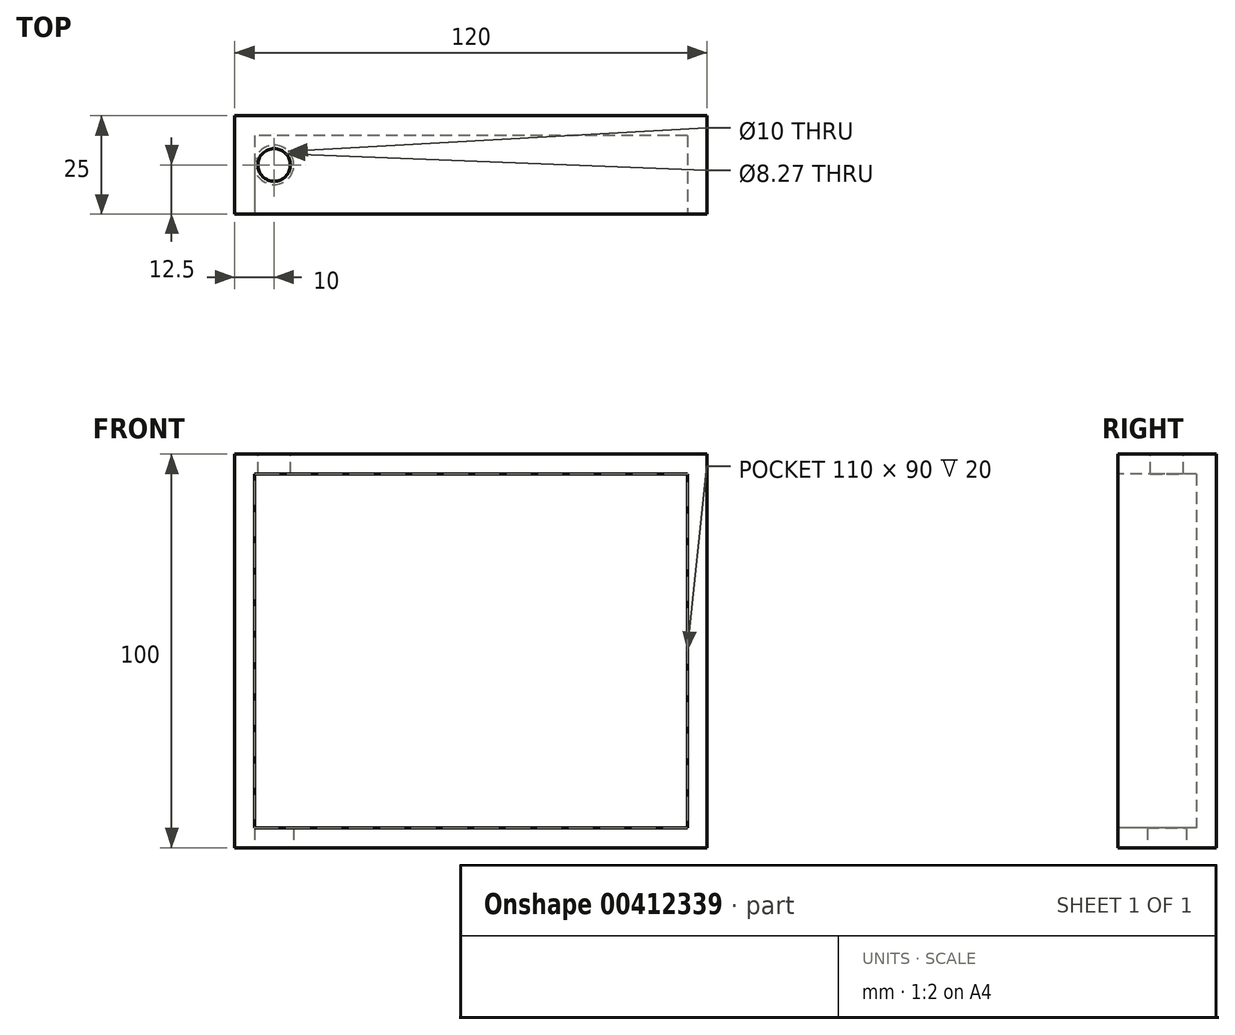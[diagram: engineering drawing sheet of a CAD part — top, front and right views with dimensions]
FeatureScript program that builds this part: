
annotation { "Feature Type Name" : "Feature", "Feature Type Description" : "" }
export const myFeature = defineFeature(function(context is Context, id is Id, definition is map)
    precondition{}
    {
        {
            var Q0;
            Q0=qCreatedBy(makeId("Front.planeOp"),FACE);
            var sketch = newSketch(context, id + "F0", { "sketchPlane" : qUnion([Q0])});
            skLineSegment(sketch, "E0.bottom", {"start": v(-60, 50) * mm, "end": v(60, 50) * mm});
            skLineSegment(sketch, "E0.top", {"start": v(-60, -50) * mm, "end": v(60, -50) * mm});
            skLineSegment(sketch, "E0.left", {"start": v(-60, 50) * mm, "end": v(-60, -50) * mm});
            skLineSegment(sketch, "E0.right", {"start": v(60, 50) * mm, "end": v(60, -50) * mm});
            skPoint(sketch, "E0.middle", {"position": v(0, 0) * mm});
            skSolve(sketch);
        }
        {
            var Q0;
            Q0=makeQuery(id+"F0.imprint","IMPRINT",FACE,{"disambiguationData":[TD([[makeQuery(id+"F0.imprint","IMPRINT",EDGE,{"derivedFrom":sQuery(id+"F0.wireOp",EDGE,"E0.bottom")}),-1.0]])]});
            extrude(context, id + "F1", {"entities" : qUnion([Q0]), "depth" : 25 * mm});
        }
        {
            var Q0;
            Q0=makeQuery(id+"F1.opExtrude","CAP_FACE",FACE,{"disambiguationData":[OSD([sQuery(id+"F0.wireOp",EDGE,"E0.bottom"),sQuery(id+"F0.wireOp",EDGE,"E0.top"),sQuery(id+"F0.wireOp",EDGE,"E0.left"),sQuery(id+"F0.wireOp",EDGE,"E0.right")])],"isStart":false});
            var sketch = newSketch(context, id + "F2", { "sketchPlane" : qUnion([Q0])});
            skLineSegment(sketch, "E1.bottom", {"start": v(55, 45) * mm, "end": v(-55, 45) * mm});
            skLineSegment(sketch, "E1.top", {"start": v(55, -45) * mm, "end": v(-55, -45) * mm});
            skLineSegment(sketch, "E1.left", {"start": v(55, 45) * mm, "end": v(55, -45) * mm});
            skLineSegment(sketch, "E1.right", {"start": v(-55, 45) * mm, "end": v(-55, -45) * mm});
            skPoint(sketch, "E1.middle", {"position": v(0, 0) * mm});
            skSolve(sketch);
        }
        {
            var Q0;
            Q0 = qSketchRegion(id + "F2", true);
            extrude(context, id + "F3", {"entities" : qUnion([Q0]), "operationType" : NewBodyOperationType.REMOVE, "oppositeDirection" : true, "depth" : 20 * mm});
        }
        {
            var Q0;
            Q0=makeQuery(id+"F1.opExtrude","SWEPT_FACE",FACE,{"disambiguationData":[OSD([sQuery(id+"F0.wireOp",EDGE,"E0.top")])]});
            var sketch = newSketch(context, id + "F4", { "sketchPlane" : qUnion([Q0])});
            skCircle(sketch, "E2", {"center": v(-50, 12.5) * mm, "radius": 5 * mm});
            skPoint(sketch, "E2.centerSnap0", {"position": v(-60, 12.5) * mm});
            skSolve(sketch);
        }
        {
            var Q0;
            Q0=makeQuery(id+"F4.imprint","IMPRINT",FACE,{"disambiguationData":[TD([[makeQuery(id+"F4.imprint","IMPRINT",EDGE,{"derivedFrom":sQuery(id+"F4.wireOp",EDGE,"E2")}),1.0]])]});
            var Q1;
            Q1=makeQuery(id+"F3.boolean.opBoolean","COPY",FACE,{"derivedFrom":makeQuery(id+"F3.opExtrude","SWEPT_FACE",FACE,{"disambiguationData":[OSD([sQuery(id+"F2.wireOp",EDGE,"E1.top")])]})});
            extrude(context, id + "F5", {"entities" : qUnion([Q0, Q1]), "operationType" : NewBodyOperationType.REMOVE, "oppositeDirection" : true, "depth" : 10 * mm});
        }
        {
            var Q0;
            Q0=makeQuery(id+"F1.opExtrude","SWEPT_FACE",FACE,{"disambiguationData":[OSD([sQuery(id+"F0.wireOp",EDGE,"E0.bottom")])]});
            var sketch = newSketch(context, id + "F6", { "sketchPlane" : qUnion([Q0])});
            skCircle(sketch, "E3", {"center": v(-50, -12.5) * mm, "radius": 4.13 * mm});
            skSolve(sketch);
        }
        {
            var Q0;
            Q0 = qSketchRegion(id + "F6", true);
            extrude(context, id + "F7", {"entities" : qUnion([Q0]), "operationType" : NewBodyOperationType.REMOVE, "oppositeDirection" : true, "depth" : 10 * mm});
        }
    });
